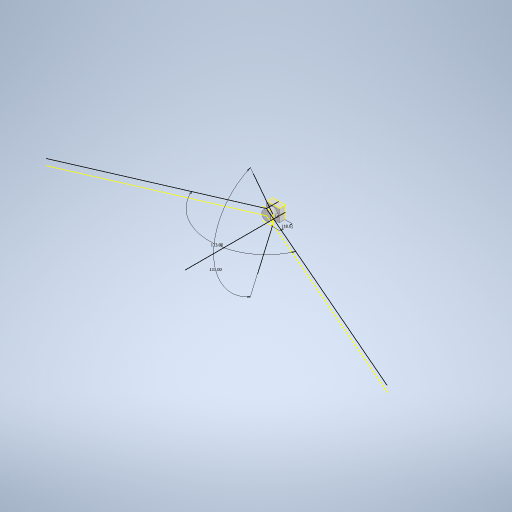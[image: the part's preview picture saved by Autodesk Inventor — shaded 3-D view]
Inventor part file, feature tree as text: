
AUTODESK INVENTOR PART (.ipt)
format: ipt  version: 2023 (Build 270158000, 158)  size: 312,320 bytes
history: native  units: in
note: dims shown in document units (in); Inventor stores cm internally (conversion verified against a paired STEP export)
features: sketch x7, projected_geometry x4, extrude x3, plane x1
ambient origin geometry x8: Origin, YZ Plane, XZ Plane, XY Plane, X Axis, Y Axis, Z Axis, Center Point
bodies: Solid1 (feature_tree)
feature tree (15):
  extrude  "Extrusion1"  Depth=0.752in
  extrude  "Extrusion2"  Depth=0.4331in
  extrude  "Extrusion3"  Depth=0.1575in
  sketch  "Sketch4"  dims[d7=0.3413in d8=0.0in]
  sketch  "Sketch5"  dims[d9=0.5512in]
  sketch  "Sketch6"  dims[d10=0.3909in d11=0.0in]
  plane  "Work Plane1"
  sketch  "Sketch7"  dims[d12=0.7323in d13=0.9139in d14=0.9139in d15=-0.376in]
  sketch  "Sketch1"  dims[d0=0.752in d1=0.752in]
  sketch  "Sketch2"  dims[d2=0.3413in d3=0.0in d4=0.4331in]
  projected_geometry  "Projected Loop1"
  sketch  "Sketch3"  dims[d5=0.0787in d6=0.1575in]
  projected_geometry  "Projected Loop2"
  projected_geometry  "Projected Loop3"
  projected_geometry  "Projected Loop4"
